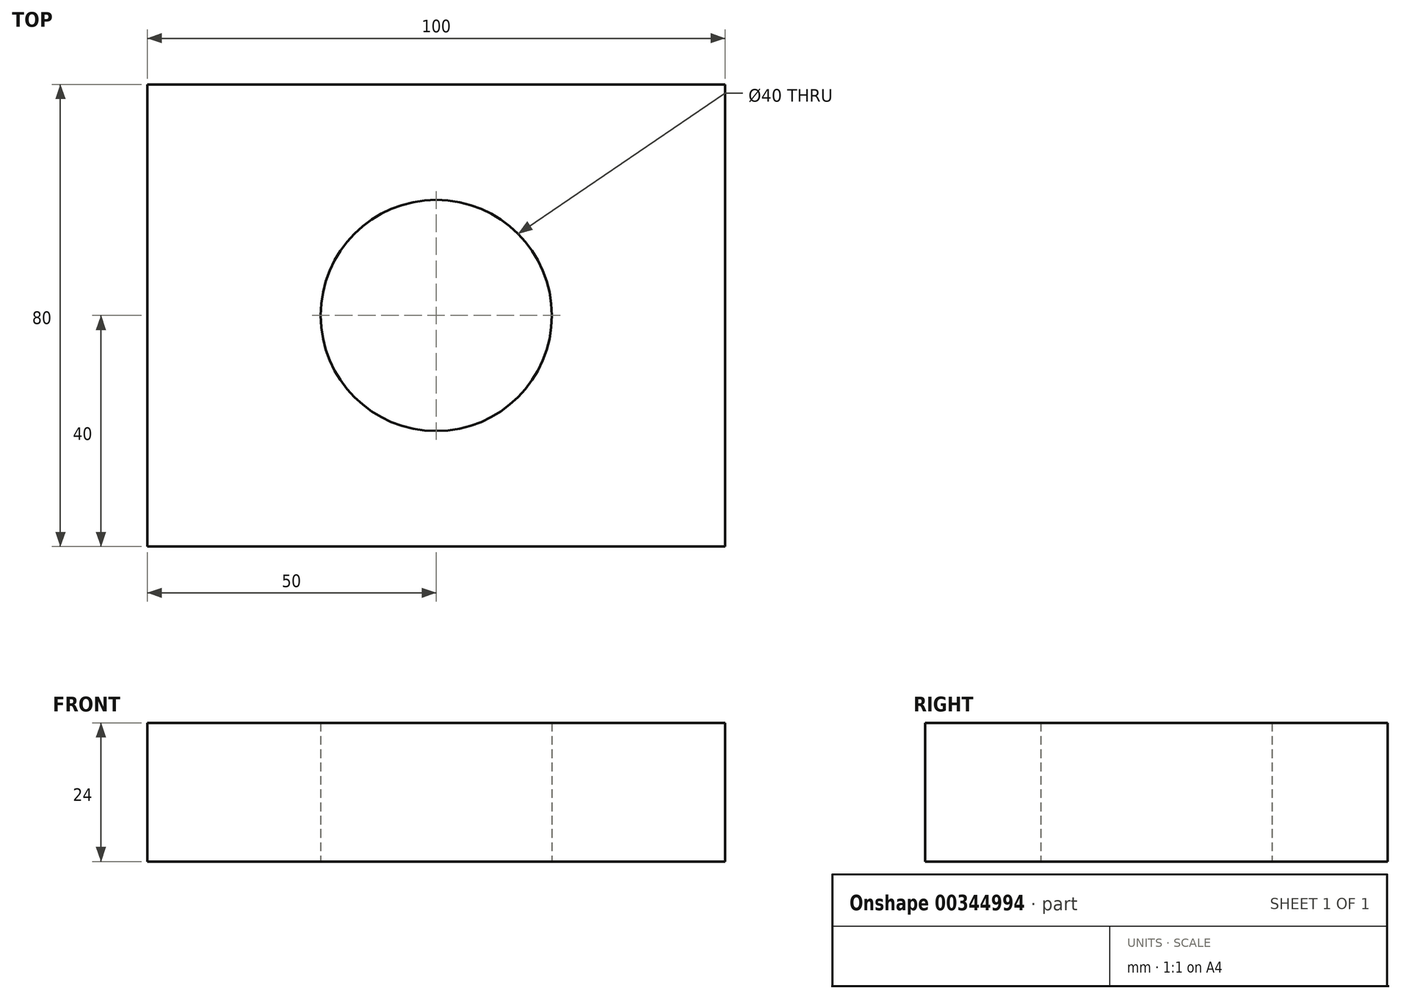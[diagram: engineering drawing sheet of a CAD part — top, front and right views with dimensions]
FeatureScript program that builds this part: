
annotation { "Feature Type Name" : "Feature", "Feature Type Description" : "" }
export const myFeature = defineFeature(function(context is Context, id is Id, definition is map)
    precondition{}
    {
        {
            var Q0;
            Q0=qCreatedBy(makeId("Top.planeOp"),FACE);
            var sketch = newSketch(context, id + "F0", { "sketchPlane" : qUnion([Q0])});
            skLineSegment(sketch, "E0.bottom", {"start": v(50, -40) * mm, "end": v(-50, -40) * mm});
            skLineSegment(sketch, "E0.top", {"start": v(50, 40) * mm, "end": v(-50, 40) * mm});
            skLineSegment(sketch, "E0.left", {"start": v(50, -40) * mm, "end": v(50, 40) * mm});
            skLineSegment(sketch, "E0.right", {"start": v(-50, -40) * mm, "end": v(-50, 40) * mm});
            skPoint(sketch, "E0.middle", {"position": v(0, 0) * mm});
            skCircle(sketch, "E1", {"center": v(0, 0) * mm, "radius": 20 * mm});
            skSolve(sketch);
        }
        {
            var Q0;
            Q0=makeQuery(id+"F0.imprint","IMPRINT",FACE,{"disambiguationData":[TD([[makeQuery(id+"F0.imprint","IMPRINT",EDGE,{"derivedFrom":sQuery(id+"F0.wireOp",EDGE,"E0.bottom")}),-1.0]])]});
            extrude(context, id + "F1", {"entities" : qUnion([Q0]), "depth" : 24 * mm});
        }
    });
